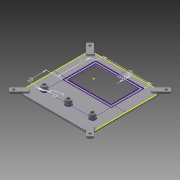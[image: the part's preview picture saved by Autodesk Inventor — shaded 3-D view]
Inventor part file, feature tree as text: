
AUTODESK INVENTOR PART (.ipt)
format: ipt  version: 2013 SP2 (Build 170200200, 200)  size: 268,288 bytes
history: native  units: mm
features: extrude x6, sketch x4, fillet x2, projected_geometry x1
ambient origin geometry x8: Origin, YZ Plane, XZ Plane, XY Plane, X Axis, Y Axis, Z Axis, Center Point
bodies: Solid1 (feature_tree)
feature tree (13):
  extrude  "Extrusion1"  Depth=8.0mm
  sketch  "Sketch2"  dims[d3=3.1mm d4=0.0mm d5=78.0mm]
  extrude  "Extrusion2"  Depth=78.0mm
  extrude  "Extrusion3"  Depth=4.0mm
  extrude  "Extrusion4"  Depth=1.5mm TaperAngle=0.0deg
  fillet  "Fillet1"  Radius=3.75mm
  fillet  "Fillet2"  Radius=4.0mm
  sketch  "Sketch4"  dims[d9=0.0mm d10=0.0mm d11=1.5mm d12=0.0mm d13=3.75mm d15=4.0mm d16=4.0mm d17=9.0mm d18=2.0mm d19=3.0mm d20=0.0mm d21=2.0mm d22=2.0mm d23=10.0mm d24=30.0mm d25=5.6mm d26=9.0mm d27=7.8mm d28=0.0mm d29=5.25mm d30=0.0mm d32=23.0mm]
  extrude  "Extrusion5"  Depth=4.0mm
  extrude  "Extrusion6"  Depth=9.0mm
  sketch  "Sketch1"  dims[d0=116.0mm d2=8.0mm]
  sketch  "Sketch3"  dims[d7=53.0mm d8=4.0mm]
  projected_geometry  "Projected Loop1"
